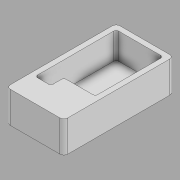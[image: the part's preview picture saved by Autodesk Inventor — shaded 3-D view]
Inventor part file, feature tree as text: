
AUTODESK INVENTOR PART (.ipt)
format: ipt  version: 2020 (Build 240168000, 168)  size: 125,952 bytes
history: native  units: in
note: dims shown in document units (in); Inventor stores cm internally (conversion verified against a paired STEP export)
features: extrude x2, sketch x2, other x1
ambient origin geometry x8: Origin, YZ Plane, XZ Plane, XY Plane, X Axis, Y Axis, Z Axis, Center Point
bodies: Body1 (feature_tree)
feature tree (5):
  other  "Sólido1"
  extrude  "Extrusión1"  Depth=4.875in
  extrude  "Extrusión2"  Depth=1.25in
  sketch  "Boceto1"  dims[d0=2.375in d1=4.875in]
  sketch  "Boceto3"  dims[d2=0.375in d3=0.375in d4=0.375in d5=0.375in d6=2.75in d7=5.25in d8=1.5in d9=0.0in d20=0.25in d21=0.25in d22=0.25in d23=1.75in d24=0.625in d25=1.5in d26=0.125in d27=1.25in d28=0.0in]
